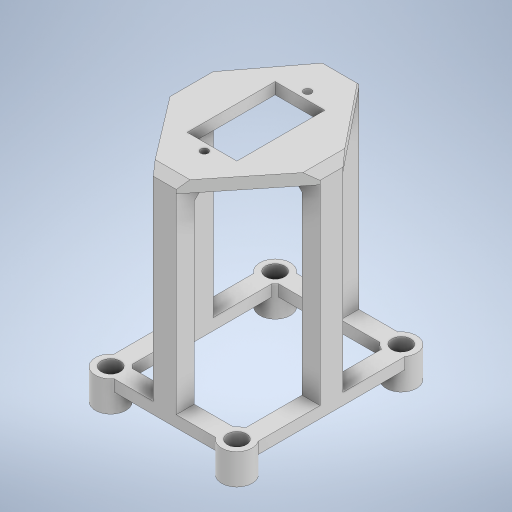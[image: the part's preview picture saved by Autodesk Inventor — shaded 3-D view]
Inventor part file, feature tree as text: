
AUTODESK INVENTOR PART (.ipt)
format: ipt  version: 2024.2 (Build 282272000, 272)  size: 406,528 bytes
history: native  units: mm
features: extrude x5, sketch x5, chamfer x2
ambient origin geometry x8: Origin, YZ Plane, XZ Plane, XY Plane, X Axis, Y Axis, Z Axis, Center Point
bodies: Solid1 (feature_tree)
feature tree (12):
  extrude  "Extrusion1"  Depth=5.0mm
  extrude  "Extrusion2"  Depth=5.0mm
  extrude  "Extrusion3"  Depth=8.0mm
  extrude  "Extrusion4"  Depth=8.0mm
  extrude  "Extrusion5"  Depth=4.0mm
  chamfer  "Chamfer1"  Distance=4.0mm
  chamfer  "Chamfer2"  Distance=4.0mm
  sketch  "Sketch1"  dims[d0=5.0mm d1=5.0mm]
  sketch  "Sketch2"  dims[d2=5.0mm d3=5.0mm]
  sketch  "Sketch3"  dims[d4=8.0mm d5=8.0mm]
  sketch  "Sketch4"  dims[d6=8.0mm d7=8.0mm]
  sketch  "Sketch5"  dims[d8=4.0mm d9=4.0mm d10=4.0mm d11=4.0mm d12=4.0mm d13=4.0mm d18=43.0mm d23=33.0mm d24=4.7mm d25=4.7mm d26=4.7mm d27=4.7mm d28=2.35mm d29=2.35mm d30=4.0mm d31=2.35mm d32=3.0mm d33=0.0mm d34=5.0mm d35=8.0mm d37=8.0mm d38=5.0mm d39=5.0mm d40=5.0mm d41=5.0mm d42=0.0mm d43=6.0mm d44=6.0mm d45=6.0mm d46=6.0mm d47=18.5mm d48=18.5mm d49=13.5mm d50=13.5mm d51=50.0mm d52=0.0mm d53=23.0mm d54=13.0mm d55=10.0mm d56=10.0mm d68=10.0mm d69=23.0mm d70=10.0mm d71=3.0mm d72=0.0mm d73=2.0mm d74=2.0mm d75=6.5mm d76=6.5mm d77=2.0mm d78=2.0mm d79=3.0mm d80=0.0mm d81=4.0mm d82=2.0mm d83=45.0deg d84=2.0mm d85=2.0mm d86=45.0deg]
